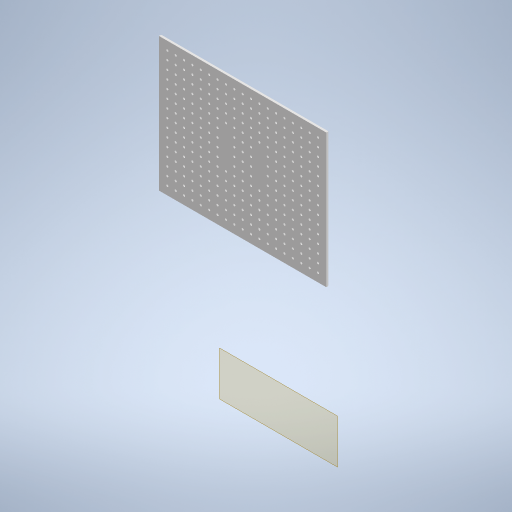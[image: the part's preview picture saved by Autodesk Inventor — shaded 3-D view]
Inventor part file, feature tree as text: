
AUTODESK INVENTOR PART (.ipt)
format: ipt  version: 2024.3 (Build 283343000, 343)  size: 825,856 bytes
history: native  units: in
note: dims shown in document units (in); Inventor stores cm internally (conversion verified against a paired STEP export)
features: other x4, extrude x3, sketch x3, fillet x2, plane x1
ambient origin geometry x8: Origin, YZ Plane, XZ Plane, XY Plane, X Axis, Y Axis, Z Axis, Center Point
bodies: Solid1 (feature_tree)
feature tree (13):
  plane  "Work Plane1"
  extrude  "Extrusion1"  Depth=0.3937in
  extrude  "Extrusion2"  Depth=0.1969in
  extrude  "Extrusion3"  Depth=0.0787in
  fillet  "Fillet2"  Radius=0.126in
  fillet  "Fillet3"  Radius=0.2756in
  sketch  "Sketch1"  dims[d0=0.3937in d1=1.9685in]
  sketch  "Sketch2"  dims[d2=1.1417in d3=0.1969in]
  sketch  "Sketch3"  dims[d4=1.378in d5=0.0in d6=0.126in d7=0.126in d8=0.2756in d9=0.2756in d10=0.8268in d11=0.1969in d12=0.0in d13=0.0in d14=9.8425in d15=7.874in d16=0.1969in d17=0.0in d19=0.126in d20=0.4921in d21=0.4921in d22=7.4803in d24=0.4921in d25=5.9055in d27=0.4921in d30=0.1181in d31=0.0787in]
  other  "<userpath>\Documents\Nauka\Studia\mgr\Semestr_3\Magisterka\uMule\mechanics\uMule-komplet.iam"
  other  "uMule-komplet.iam"
  other  "uMule-power_pack:1"
  other  "uMule-battery_case:1"
